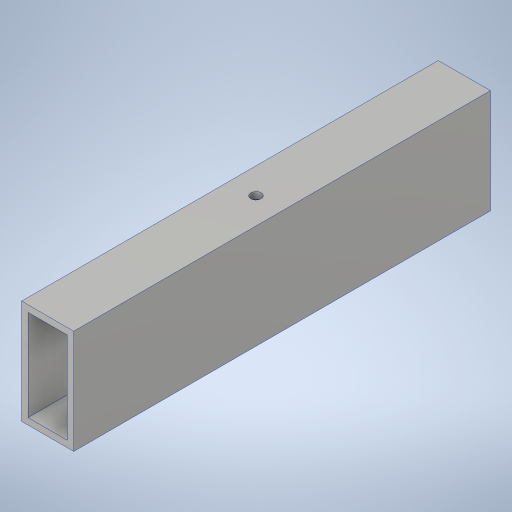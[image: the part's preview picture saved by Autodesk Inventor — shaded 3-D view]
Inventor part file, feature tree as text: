
AUTODESK INVENTOR PART (.ipt)
format: ipt  version: 2023.4 (Build 274418000, 418)  size: 230,400 bytes
history: native  units: in
note: dims shown in document units (in); Inventor stores cm internally (conversion verified against a paired STEP export)
features: extrude x1, hole x1, sketch x1
ambient origin geometry x8: Origin, YZ Plane, XZ Plane, XY Plane, X Axis, Y Axis, Z Axis, Center Point
bodies: Solid1 (feature_tree)
feature tree (3):
  extrude  "Extrusion1"  [1 undecoded]
  hole  "Hole1"  [1 undecoded]
  sketch  "Sketch2"  dims[d4=0.0in d5=0.201in d6=0.75in d7=0.385in d8=0.25in d9=0.5635in d10=1.0in d11=0.8108in]
note: 2 required parameter values undecoded (feature->parameter linkage not recoverable at this tier; creation-order binding heuristic only, values carry confidence <= 0.55)
